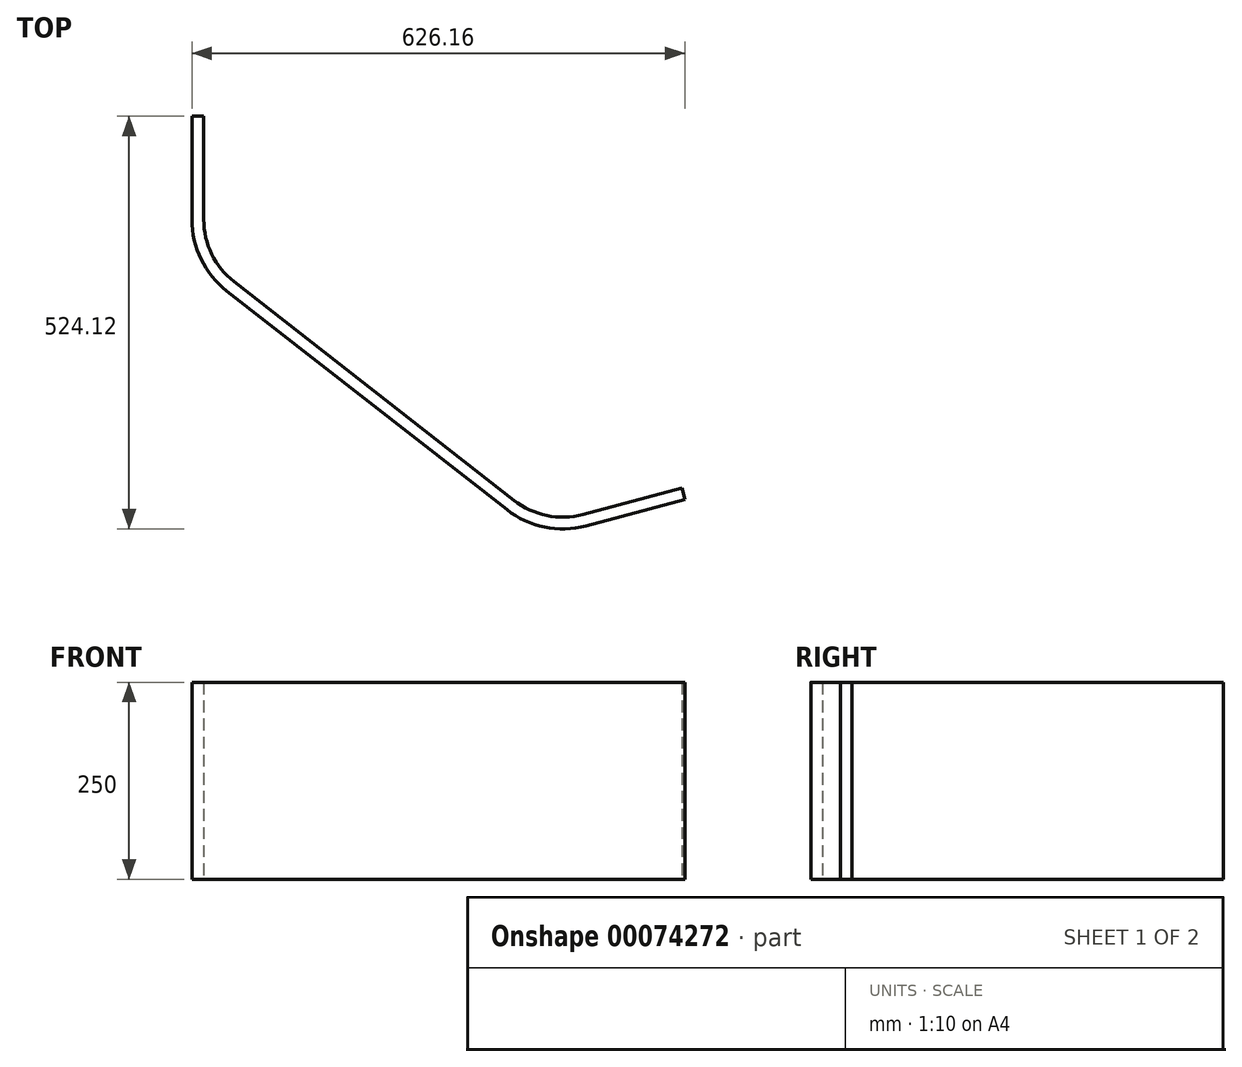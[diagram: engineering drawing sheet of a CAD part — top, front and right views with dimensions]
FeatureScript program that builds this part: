
annotation { "Feature Type Name" : "Feature", "Feature Type Description" : "" }
export const myFeature = defineFeature(function(context is Context, id is Id, definition is map)
    precondition{}
    {
        {
            var Q0;
            Q0=qCreatedBy(makeId("Top.planeOp"),FACE);
            var sketch = newSketch(context, id + "F0", { "sketchPlane" : qUnion([Q0])});
            skLineSegment(sketch, "E0", {"start": v(439.8, -487.29) * mm, "end": v(565.52, -453.6) * mm});
            skLineSegment(sketch, "E1", {"start": v(352.36, -469.5) * mm, "end": v(-3.32, -191.6) * mm});
            skLineSegment(sketch, "E2", {"start": v(155.3, -18.17) * mm, "end": v(147.32, -23.49) * mm});
            skLineSegment(sketch, "E3", {"start": v(-41.76, -112.8) * mm, "end": v(-41.76, 18.42) * mm});
            skPoint(sketch, "E4.visualSharp", {"position": v(-41.76, -161.58) * mm});
            skArc(sketch, "E4.filletArc", {"start": v(-41.76, -112.8) * mm, "mid": v(-31.64, -156.64) * mm, "end": v(-3.32, -191.6) * mm});
            skPoint(sketch, "E5.visualSharp", {"position": v(391.65, -500.2) * mm});
            skArc(sketch, "E5.filletArc", {"start": v(352.36, -469.5) * mm, "mid": v(394, -488.69) * mm, "end": v(439.8, -487.29) * mm});
            skLineSegment(sketch, "E6.0", {"start": v(-56.76, -112.8) * mm, "end": v(-56.76, 18.42) * mm});
            skLineSegment(sketch, "E6.1", {"start": v(443.7, -501.78) * mm, "end": v(569.4, -468.1) * mm});
            skArc(sketch, "E6.2", {"start": v(343.13, -481.32) * mm, "mid": v(391, -503.39) * mm, "end": v(443.7, -501.78) * mm});
            skLineSegment(sketch, "E6.3", {"start": v(343.13, -481.32) * mm, "end": v(-12.56, -203.43) * mm});
            skArc(sketch, "E6.4", {"start": v(-56.76, -112.8) * mm, "mid": v(-45.12, -163.22) * mm, "end": v(-12.56, -203.43) * mm});
            skLineSegment(sketch, "E7", {"start": v(-56.76, 18.42) * mm, "end": v(-41.76, 18.42) * mm});
            skLineSegment(sketch, "E8", {"start": v(569.4, -468.1) * mm, "end": v(565.52, -453.6) * mm});
            skLineSegment(sketch, "E9", {"start": v(443.7, -501.78) * mm, "end": v(1799.96, -501.78) * mm, "construction": true});
            skCircle(sketch, "E10", {"center": v(846.93, -324.28) * mm, "radius": 257.5 * mm, "construction": true});
            skLineSegment(sketch, "E11", {"start": v(-247.56, -324.28) * mm, "end": v(1865.67, -324.28) * mm, "construction": true});
            skLineSegment(sketch, "E12", {"start": v(904.4, -581.78) * mm, "end": v(-204.7, -581.78) * mm, "construction": true});
            skLineSegment(sketch, "E13", {"start": v(-41.76, 18.42) * mm, "end": v(-41.76, -607.23) * mm, "construction": true});
            skSolve(sketch);
        }
        {
            var Q0;
            Q0 = qSketchRegion(id + "F0", true);
            extrude(context, id + "F1", {"entities" : qUnion([Q0]), "depth" : 250 * mm});
        }
    });
